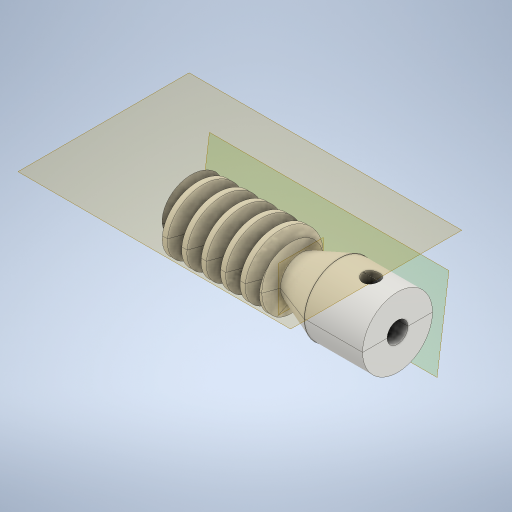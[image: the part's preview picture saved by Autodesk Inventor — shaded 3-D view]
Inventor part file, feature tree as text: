
AUTODESK INVENTOR PART (.ipt)
format: ipt  version: 2023.1 (Build 271208000, 208)  size: 547,840 bytes
history: native  units: mm (DEFAULTED — no unit token found)
features: other x11, sketch x6, plane x5, extrude x4, chamfer x2, pattern_circular x2, hole x1, split x1
ambient origin geometry x6: Origin, XZ Plane, X Axis, Y Axis, Z Axis, Center Point
bodies: Solid1 (feature_tree), Solid2 (feature_tree), Solid3 (feature_tree)
feature tree (32):
  extrude  "Base Body"  Depth=17.6mm
  chamfer  "Chamfer1"  Distance=3.52mm
  chamfer  "Chamfer2"  Distance=19.198622mm
  other  "Tooth Sketch"
  other  "Tooth"
  pattern_circular  "Tooth Pattern"  [2 undecoded]
  other  "Left Tooth"
  pattern_circular  "Left Tooth Pattern"  [2 undecoded]
  plane  "Work Plane10"
  extrude  "Extrusion2"  Depth=17.592919mm
  extrude  "Extrusion3"  Depth=10.0mm
  extrude  "Extrusion4"  Depth=5.28mm
  plane  "Work Plane12"
  plane  "Work Plane13"
  plane  "Work Plane14"
  hole  "Hole1"  [1 undecoded]
  split  "Split1"
  other  "Base Body Sketch"
  sketch  "Sketch5"  dims[d4=40.0mm d5=17.6mm]
  other  "Srf1"
  sketch  "Sketch6"  dims[d6=30.0mm]
  sketch  "Sketch7"  dims[d7=0.0mm]
  sketch  "Sketch8"  dims[d8=1.281175mm]
  plane  "Work Plane11"
  sketch  "Sketch10"  dims[d9=3.52mm]
  sketch  "Sketch11"  dims[d10=1.281175mm d11=3.52mm d12=19.198622mm d14=3.1425mm d24=19.198622mm d25=17.592919mm d26=1.256637mm d27=5.28mm d28=7.2mm d29=8.888mm d30=5.026548mm d31=10.0mm d32=80.0mm d33=0.0mm d34=90.0deg d35=90.0deg d36=0.0mm d37=0.0mm d44=10.0mm d46=360.0deg d47=45.0deg d48=45.0deg d49=51.477061mm d50=0.0mm d54=0.0mm d56=0.0mm d59=14.4mm d60=10.0mm d61=0.0mm d62=5.026548mm d63=10.0mm d64=80.0mm d65=0.0mm d66=90.0deg d67=90.0deg d68=0.0mm d69=0.0mm d70=10.0mm d71=10.0mm d72=10.0mm d73=360.0deg d75=10.0mm d76=10.0mm d77=0.0mm d79=51.477061mm d80=0.0mm d81=0.0mm d82=10.0mm d83=3.665191mm d84=15.0mm d85=0.0mm d86=5.4mm d87=17.75mm d88=0.0mm d89=18.048284mm d93=0.5mm d94=0.0mm d95=9.024mm d96=4.3mm d97=4.3mm d98=6.0mm d99=4.0mm d100=2.0mm d101=90.0deg d102=10.0mm d103=0.0mm d90=0.5mm d91=0.872665mm d92=0.5mm d104=0.0625mm d105=0.75mm d106=0.375mm]
  other  "Pitch Diameter"
  other  "G:\Assembly1.iam"
  other  "Assembly1.iam"
  other  "Nema17:1"
  other  "axis:1"
  other  "header:1"
note: 5 required parameter values undecoded (feature->parameter linkage not recoverable at this tier; creation-order binding heuristic only, values carry confidence <= 0.55)
